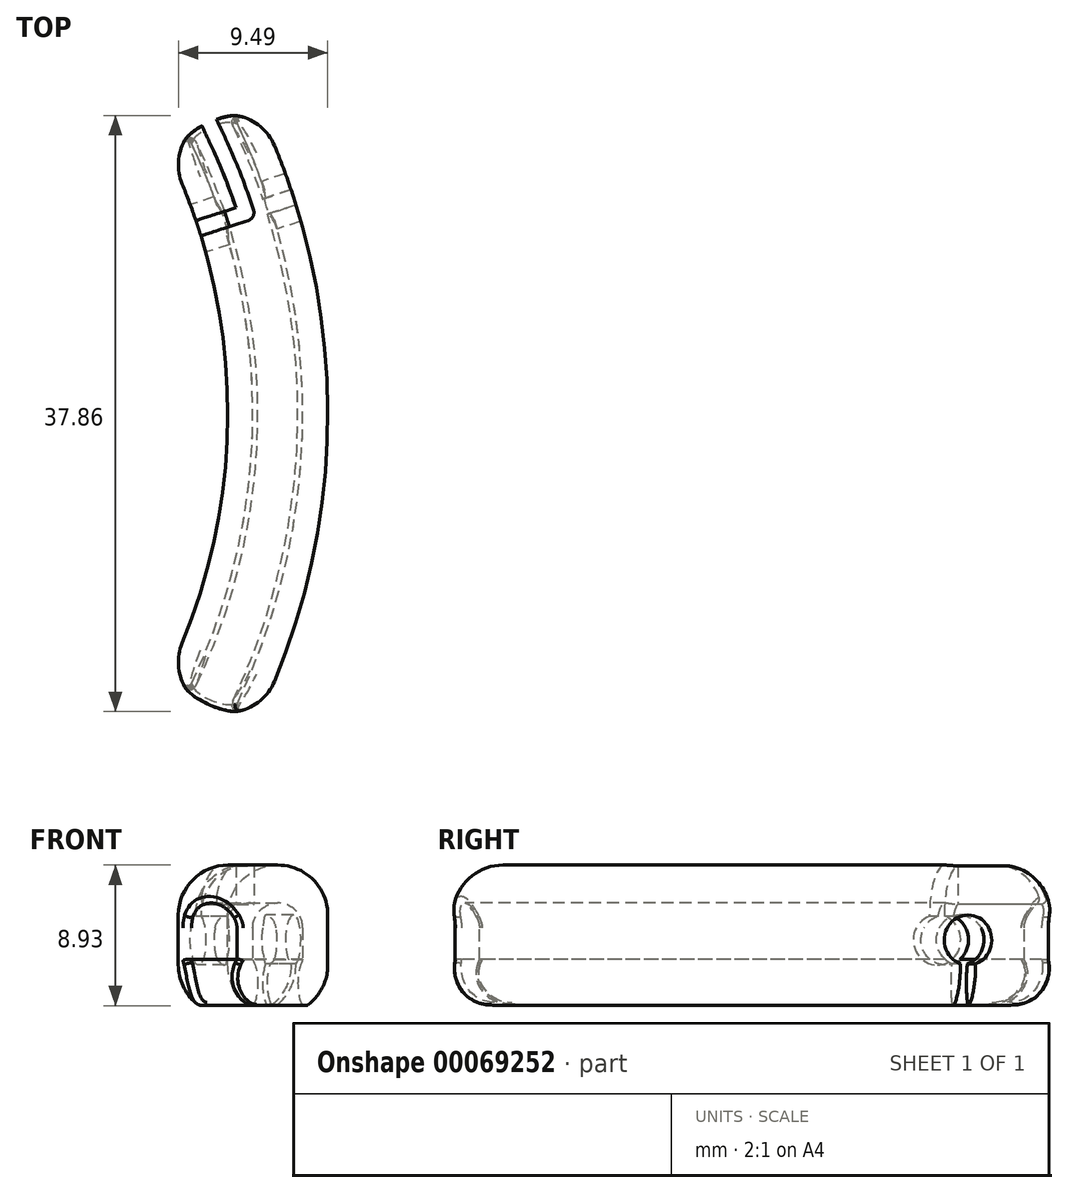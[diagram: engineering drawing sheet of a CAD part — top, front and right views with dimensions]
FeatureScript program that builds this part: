
annotation { "Feature Type Name" : "Feature", "Feature Type Description" : "" }
export const myFeature = defineFeature(function(context is Context, id is Id, definition is map)
    precondition{}
    {
        {
            var Q0;
            Q0=qCreatedBy(makeId("Front.planeOp"),FACE);
            var sketch = newSketch(context, id + "F0", { "sketchPlane" : qUnion([Q0])});
            skLineSegment(sketch, "E0", {"start": v(38.1, -1.59) * mm, "end": v(38.1, 1.59) * mm});
            skLineSegment(sketch, "E1", {"start": v(44.45, 1.59) * mm, "end": v(44.45, -1.59) * mm});
            skArc(sketch, "E2", {"start": v(44.45, 1.59) * mm, "mid": v(41.28, 4.76) * mm, "end": v(38.1, 1.59) * mm});
            skArc(sketch, "E3", {"start": v(38.1, -1.59) * mm, "mid": v(41.28, -4.76) * mm, "end": v(44.45, -1.59) * mm});
            skLineSegment(sketch, "E4", {"start": v(0, 0) * mm, "end": v(0, -27.8) * mm});
            skSolve(sketch);
        }
        {
            var Q0;
            Q0=makeQuery(id+"F0.imprint","IMPRINT",FACE,{"disambiguationData":[TD([[makeQuery(id+"F0.imprint","IMPRINT",EDGE,{"derivedFrom":sQuery(id+"F0.wireOp",EDGE,"E0")}),-1.0]])]});
            var Q1;
            Q1=sQuery(id+"F0.wireOp",EDGE,"E4");
            revolve(context, id + "F1", {"entities" : qUnion([Q0]), "axis" : qUnion([Q1]), "revolveType" : RevolveType.SYMMETRIC, "angle" : 45 * degree});
        }
        {
            var Q0;
            Q0=makeQuery(id+"F1.opRevolve","CAP_FACE",FACE,{"disambiguationData":[OSD([sQuery(id+"F0.wireOp",EDGE,"E0"),sQuery(id+"F0.wireOp",EDGE,"E1"),sQuery(id+"F0.wireOp",EDGE,"E2"),sQuery(id+"F0.wireOp",EDGE,"E3")])],"isStart":false});
            var sketch = newSketch(context, id + "F2", { "sketchPlane" : qUnion([Q0])});
            skLineSegment(sketch, "E5", {"start": v(41.28, 4.76) * mm, "end": v(41.28, -4.76) * mm});
            skSolve(sketch);
        }
        {
            var Q0;
            Q0=qSketchRegion(id+"F2",true);
            var Q1;
            {var subQ0=sQuery(id+"F2.wireOp",EDGE,"E5");Q1=makeQuery(id+"F2.imprint","IMPRINT",FACE,{"disambiguationData":[TD([[makeQuery(id+"F2.imprint","IMPRINT",EDGE,{"derivedFrom":subQ0}),1.0]])]});}
            var Q2;
            Q2=sQuery(id+"F2.wireOp",EDGE,"E5");
            revolve(context, id + "F3", {"operationType" : NewBodyOperationType.ADD, "entities" : qUnion([Q0, Q1]), "axis" : qUnion([Q2]), "revolveType" : RevolveType.FULL});
        }
        {
            var Q0;
            Q0=makeQuery(id+"F1.opRevolve","CAP_FACE",FACE,{"disambiguationData":[OSD([sQuery(id+"F0.wireOp",EDGE,"E0"),sQuery(id+"F0.wireOp",EDGE,"E1"),sQuery(id+"F0.wireOp",EDGE,"E2"),sQuery(id+"F0.wireOp",EDGE,"E3")])],"isStart":true});
            var sketch = newSketch(context, id + "F4", { "sketchPlane" : qUnion([Q0])});
            skLineSegment(sketch, "E6", {"start": v(-41.28, 4.76) * mm, "end": v(-41.28, -4.76) * mm});
            skSolve(sketch);
        }
        {
            var Q0;
            Q0=qSketchRegion(id+"F4",true);
            var Q1;
            {var subQ0=sQuery(id+"F4.wireOp",EDGE,"E6");Q1=makeQuery(id+"F4.imprint","IMPRINT",FACE,{"disambiguationData":[TD([[makeQuery(id+"F4.imprint","IMPRINT",EDGE,{"derivedFrom":subQ0}),1.0]])]});}
            var Q2;
            Q2=sQuery(id+"F4.wireOp",EDGE,"E6");
            revolve(context, id + "F5", {"operationType" : NewBodyOperationType.ADD, "entities" : qUnion([Q0, Q1]), "axis" : qUnion([Q2]), "revolveType" : RevolveType.FULL});
        }
        {
            var Q0;
            Q0=qCreatedBy(makeId("Front.planeOp"),FACE);
            var sketch = newSketch(context, id + "F6", { "sketchPlane" : qUnion([Q0])});
            skLineSegment(sketch, "E7", {"start": v(38.13, 4.76) * mm, "end": v(41.28, 4.76) * mm});
            skArc(sketch, "E8", {"start": v(41.28, 4.76) * mm, "mid": v(39.03, 3.83) * mm, "end": v(38.1, 1.59) * mm});
            skLineSegment(sketch, "E9", {"start": v(44.45, 1.59) * mm, "end": v(44.45, -1.59) * mm});
            skLineSegment(sketch, "E10", {"start": v(38.13, -4.76) * mm, "end": v(41.28, -4.76) * mm});
            skArc(sketch, "E11", {"start": v(38.1, -1.59) * mm, "mid": v(39.03, -3.83) * mm, "end": v(41.28, -4.76) * mm});
            skLineSegment(sketch, "E12", {"start": v(41.28, 4.76) * mm, "end": v(41.28, -4.76) * mm, "construction": true});
            skLineSegment(sketch, "E13", {"start": v(0, 0) * mm, "end": v(48.62, 0) * mm, "construction": true});
            skPoint(sketch, "E13.endSnap0", {"position": v(44.45, 0) * mm});
            skLineSegment(sketch, "E14", {"start": v(39.69, -6.35) * mm, "end": v(39.69, 0.76) * mm});
            skLineSegment(sketch, "E15", {"start": v(42.86, -6.35) * mm, "end": v(42.86, 0.76) * mm});
            skLineSegment(sketch, "E16", {"start": v(39.69, -6.35) * mm, "end": v(42.86, -6.35) * mm});
            skArc(sketch, "E17", {"start": v(42.86, 0.76) * mm, "mid": v(41.28, 2.35) * mm, "end": v(39.69, 0.76) * mm});
            skLineSegment(sketch, "E18", {"start": v(0, 0) * mm, "end": v(0, -11.33) * mm, "construction": true});
            skArc(sketch, "E19", {"start": v(39.69, -4.28) * mm, "mid": v(40, -2.76) * mm, "end": v(39.69, -1.23) * mm});
            skArc(sketch, "E20", {"start": v(42.86, -1.23) * mm, "mid": v(42.55, -2.76) * mm, "end": v(42.86, -4.28) * mm});
            skLineSegment(sketch, "E21", {"start": v(39.69, -1.23) * mm, "end": v(42.86, -1.23) * mm, "construction": true});
            skLineSegment(sketch, "E22", {"start": v(39.69, -4.28) * mm, "end": v(42.86, -4.28) * mm, "construction": true});
            skSolve(sketch);
        }
        {
            var Q0;
            {var subQ0=sQuery(id+"F6.wireOp",EDGE,"E11");var subQ1=sQuery(id+"F6.wireOp",EDGE,"E10");var subQ2=makeQuery(id+"F6.imprint","INTERSECT",VERTEX,{"derivedFrom":[subQ1,subQ0]});Q0=makeQuery(id+"F6.imprint","IMPRINT",FACE,{"disambiguationData":[TD([[makeQuery(id+"F6.imprint","IMPRINT",EDGE,{"disambiguationData":[TD([[subQ2,1.0]])],"derivedFrom":subQ1}),1.0]])]});}
            var Q1;
            Q1=makeQuery(id+"F6.imprint","IMPRINT",FACE,{"disambiguationData":[TD([[makeQuery(id+"F6.imprint","IMPRINT",EDGE,{"derivedFrom":sQuery(id+"F6.wireOp",EDGE,"E15")}),1.0]])]});
            var Q2;
            Q2=sQuery(id+"F6.wireOp",EDGE,"E18");
            revolve(context, id + "F7", {"operationType" : NewBodyOperationType.REMOVE, "entities" : qUnion([Q0, Q1]), "axis" : qUnion([Q2]), "revolveType" : RevolveType.FULL, "oppositeDirection" : true});
        }
        {
            var Q0;
            Q0=qCreatedBy(makeId("Top.planeOp"),FACE);
            var sketch = newSketch(context, id + "F8", { "sketchPlane" : qUnion([Q0])});
            skArc(sketch, "E23.0", {"start": v(41.07, -17.01) * mm, "mid": v(44.45, 0) * mm, "end": v(41.07, 17.01) * mm});
            skLineSegment(sketch, "E24.0", {"start": v(41.07, 17.01) * mm, "end": v(35.2, 14.58) * mm});
            skFitSpline(sketch, "E25.0", {"points": [v(35.7, 17.84) * mm, v(35.8, 17.96) * mm, v(35.96, 18.09) * mm, v(36.16, 18.22) * mm, v(36.37, 18.36) * mm, v(36.6, 18.48) * mm, v(36.85, 18.6) * mm, v(37.1, 18.72) * mm, v(37.35, 18.8) * mm, v(37.59, 18.87) * mm, v(37.82, 18.94) * mm, v(38.02, 18.97) * mm, v(38.18, 18.97) * mm]});
            skPoint(sketch, "E26.startSnap0", {"position": v(38.13, 15.8) * mm});
            skCircle(sketch, "E27", {"center": v(0, 0) * mm, "radius": 41.28 * mm, "construction": true});
            skLineSegment(sketch, "E28", {"start": v(0, 0) * mm, "end": v(47.07, 15.3) * mm, "construction": true});
            skArc(sketch, "E29", {"start": v(38.77, 12.6) * mm, "mid": v(37.24, 16.58) * mm, "end": v(35.3, 20.38) * mm});
            skArc(sketch, "E30", {"start": v(39.74, 12.91) * mm, "mid": v(38.17, 17) * mm, "end": v(36.19, 20.9) * mm});
            skArc(sketch, "E31", {"start": v(38.77, 12.6) * mm, "mid": v(39.41, 12.27) * mm, "end": v(39.74, 12.91) * mm});
            skLineSegment(sketch, "E32", {"start": v(35.3, 20.38) * mm, "end": v(36.19, 20.9) * mm});
            skSolve(sketch);
        }
        {
            var Q0;
            Q0=qSketchRegion(id+"F8",true);
            extrude(context, id + "F9", {"entities" : qUnion([Q0]), "operationType" : NewBodyOperationType.REMOVE, "endBound" : BoundingType.THROUGH_ALL, "depth" : 25.4 * mm});
        }
        {
            var Q0;
            Q0=sQuery(id+"F8.wireOp",VERTEX,"E30.center");
            var Q1;
            Q1=sQuery(id+"F8.wireOp",EDGE,"E28");
            cPlane(context, id + "F10", {"entities" : qUnion([Q0, Q1]), "cplaneType" : CPlaneType.LINE_POINT, "offset" : 152.4 * mm, "width" : 152.4 * mm, "height" : 152.4 * mm});
        }
        {
            var Q0;
            Q0=qCreatedBy(id+"F10.planeOp",FACE);
            var sketch = newSketch(context, id + "F11", { "sketchPlane" : qUnion([Q0])});
            skPoint(sketch, "E33", {"position": v(0, 0) * mm});
            skSolve(sketch);
        }
        {
            var Q0;
            Q0=sQuery(id+"F11.wireOp",VERTEX,"E33");
            var Q1;
            Q1=makeQuery(id+"F1.opRevolve","SWEPT_BODY",BODY,{"disambiguationData":[OSD([sQuery(id+"F0.wireOp",EDGE,"E0"),sQuery(id+"F0.wireOp",EDGE,"E1"),sQuery(id+"F0.wireOp",EDGE,"E2"),sQuery(id+"F0.wireOp",EDGE,"E3")])]});
            hole(context, id + "F12", {"style" : HoleStyle.SIMPLE, "holeDiameter" : 3.17 * mm, "endStyle" : HoleEndStyle.THROUGH, "oppositeDirection" : true, "locations" : qUnion([Q0]), "scope" : qUnion([Q1])});
        }
        {
            var Q0;
            Q0=qCreatedBy(makeId("Top.planeOp"),FACE);
            var sketch = newSketch(context, id + "F13", { "sketchPlane" : qUnion([Q0])});
            skArc(sketch, "E34.0", {"start": v(38.77, 12.6) * mm, "mid": v(39.41, 12.27) * mm, "end": v(39.74, 12.91) * mm});
            skLineSegment(sketch, "E35", {"start": v(40.25, 14.75) * mm, "end": v(41.76, 15.24) * mm});
            skLineSegment(sketch, "E36", {"start": v(42.74, 12.22) * mm, "end": v(41.23, 11.73) * mm});
            skLineSegment(sketch, "E37", {"start": v(35.71, 13.27) * mm, "end": v(37.22, 13.76) * mm});
            skLineSegment(sketch, "E38", {"start": v(38.2, 10.74) * mm, "end": v(36.7, 10.25) * mm});
            skLineSegment(sketch, "E39", {"start": v(35.47, 12.06) * mm, "end": v(39.1, 13.24) * mm});
            skLineSegment(sketch, "E40", {"start": v(39.1, 13.24) * mm, "end": v(39.41, 12.27) * mm});
            skLineSegment(sketch, "E41", {"start": v(39.41, 12.27) * mm, "end": v(35.78, 11.1) * mm});
            skLineSegment(sketch, "E42", {"start": v(35.78, 11.1) * mm, "end": v(35.47, 12.06) * mm});
            skLineSegment(sketch, "E43", {"start": v(35.63, 11.58) * mm, "end": v(39.25, 12.75) * mm, "construction": true});
            skSolve(sketch);
        }
        {
            var Q0;
            Q0=qSketchRegion(id+"F13",true);
            extrude(context, id + "F14", {"entities" : qUnion([Q0]), "operationType" : NewBodyOperationType.REMOVE, "endBound" : BoundingType.THROUGH_ALL, "depth" : 25.4 * mm});
        }
        {
            var Q0;
            Q0=qCreatedBy(makeId("Top.planeOp"),FACE);
            var sketch = newSketch(context, id + "F15", { "sketchPlane" : qUnion([Q0])});
            skLineSegment(sketch, "E44", {"start": v(39.1, 13.24) * mm, "end": v(39.41, 12.27) * mm});
            skLineSegment(sketch, "E45", {"start": v(39.41, 12.27) * mm, "end": v(43.04, 13.45) * mm});
            skLineSegment(sketch, "E46", {"start": v(43.04, 13.45) * mm, "end": v(42.72, 14.42) * mm});
            skLineSegment(sketch, "E47", {"start": v(42.72, 14.42) * mm, "end": v(39.1, 13.24) * mm});
            skSolve(sketch);
        }
        {
            var Q0;
            Q0=qSketchRegion(id+"F15",true);
            extrude(context, id + "F16", {"entities" : qUnion([Q0]), "operationType" : NewBodyOperationType.REMOVE, "endBound" : BoundingType.THROUGH_ALL, "oppositeDirection" : true, "depth" : 25.4 * mm});
        }
        {
            var Q0;
            {var subQ0=sQuery(id+"F0.wireOp",EDGE,"E3");var subQ1=makeQuery(id+"F1.opRevolve","SWEPT_FACE",FACE,{"disambiguationData":[OSD([subQ0])]});var subQ2=sQuery(id+"F6.wireOp",EDGE,"E15");var subQ3=makeQuery(id+"F7.opRevolve","SWEPT_FACE",FACE,{"disambiguationData":[OSD([subQ2]),TDD([makeQuery(id+"F6.imprint","IMPRINT",EDGE,{"disambiguationData":[TD([[makeQuery(id+"F6.imprint","INTERSECT",VERTEX,{"derivedFrom":[subQ2,sQuery(id+"F6.wireOp",EDGE,"E16")]}),-1.0]])],"derivedFrom":subQ2})])]});Q0=makeQuery(id+"F16.boolean.opBoolean","SPLIT",EDGE,{"disambiguationData":[TD([makeQuery(id+"F3.opRevolve","SWEPT_FACE",FACE,{"disambiguationData":[OSD([subQ0])]})])],"derivedFrom":makeQuery(id+"F7.boolean.opBoolean","INTERSECT",EDGE,{"derivedFrom":[subQ1,subQ3]})});}
            var Q1;
            {var subQ0=sQuery(id+"F0.wireOp",EDGE,"E3");var subQ1=makeQuery(id+"F1.opRevolve","SWEPT_FACE",FACE,{"disambiguationData":[OSD([subQ0])]});var subQ2=sQuery(id+"F6.wireOp",EDGE,"E15");var subQ3=makeQuery(id+"F7.opRevolve","SWEPT_FACE",FACE,{"disambiguationData":[OSD([subQ2]),TDD([makeQuery(id+"F6.imprint","IMPRINT",EDGE,{"disambiguationData":[TD([[makeQuery(id+"F6.imprint","INTERSECT",VERTEX,{"derivedFrom":[subQ2,sQuery(id+"F6.wireOp",EDGE,"E16")]}),-1.0]])],"derivedFrom":subQ2})])]});Q1=makeQuery(id+"F16.boolean.opBoolean","SPLIT",EDGE,{"disambiguationData":[TD([makeQuery(id+"F5.opRevolve","SWEPT_FACE",FACE,{"disambiguationData":[OSD([subQ0])]})])],"derivedFrom":makeQuery(id+"F7.boolean.opBoolean","INTERSECT",EDGE,{"derivedFrom":[subQ1,subQ3]})});}
            var Q2;
            {var subQ0=sQuery(id+"F6.wireOp",EDGE,"E15");Q2=makeQuery(id+"F7.boolean.opBoolean","INTERSECT",EDGE,{"derivedFrom":[makeQuery(id+"F5.opRevolve","SWEPT_FACE",FACE,{"disambiguationData":[OSD([sQuery(id+"F0.wireOp",EDGE,"E3")])]}),makeQuery(id+"F7.opRevolve","SWEPT_FACE",FACE,{"disambiguationData":[OSD([subQ0]),TDD([makeQuery(id+"F6.imprint","IMPRINT",EDGE,{"disambiguationData":[TD([[makeQuery(id+"F6.imprint","INTERSECT",VERTEX,{"derivedFrom":[subQ0,sQuery(id+"F6.wireOp",EDGE,"E16")]}),-1.0]])],"derivedFrom":subQ0})])]})]});}
            var Q3;
            {var subQ0=sQuery(id+"F6.wireOp",EDGE,"E14");var subQ2=makeQuery(id+"F6.imprint","INTERSECT",VERTEX,{"derivedFrom":[sQuery(id+"F6.wireOp",EDGE,"E10"),subQ0]});Q3=makeQuery(id+"F7.boolean.opBoolean","INTERSECT",EDGE,{"derivedFrom":[makeQuery(id+"F5.opRevolve","SWEPT_FACE",FACE,{"disambiguationData":[OSD([sQuery(id+"F0.wireOp",EDGE,"E3")])]}),makeQuery(id+"F7.opRevolve","SWEPT_FACE",FACE,{"disambiguationData":[OSD([subQ0]),TDD([makeQuery(id+"F6.imprint","IMPRINT",EDGE,{"disambiguationData":[TD([[makeQuery(id+"F6.imprint","INTERSECT",VERTEX,{"derivedFrom":[subQ0,sQuery(id+"F6.wireOp",EDGE,"E16")]}),-1.0]])],"derivedFrom":subQ0}),makeQuery(id+"F6.imprint","IMPRINT",EDGE,{"disambiguationData":[TD([[subQ2,-1.0]])],"derivedFrom":subQ0}),makeQuery(id+"F6.imprint","IMPRINT",EDGE,{"disambiguationData":[TD([[makeQuery(id+"F6.imprint","INTERSECT",VERTEX,{"disambiguationData":[OD(0.0)],"derivedFrom":[subQ0,sQuery(id+"F6.wireOp",EDGE,"E19")]}),1.0]])],"derivedFrom":subQ0})])]})]});}
            var Q4;
            {var subQ0=sQuery(id+"F6.wireOp",EDGE,"E14");var subQ2=makeQuery(id+"F6.imprint","INTERSECT",VERTEX,{"derivedFrom":[sQuery(id+"F6.wireOp",EDGE,"E10"),subQ0]});Q4=makeQuery(id+"F7.boolean.opBoolean","INTERSECT",EDGE,{"derivedFrom":[makeQuery(id+"F1.opRevolve","SWEPT_FACE",FACE,{"disambiguationData":[OSD([sQuery(id+"F0.wireOp",EDGE,"E3")])]}),makeQuery(id+"F7.opRevolve","SWEPT_FACE",FACE,{"disambiguationData":[OSD([subQ0]),TDD([makeQuery(id+"F6.imprint","IMPRINT",EDGE,{"disambiguationData":[TD([[makeQuery(id+"F6.imprint","INTERSECT",VERTEX,{"derivedFrom":[subQ0,sQuery(id+"F6.wireOp",EDGE,"E16")]}),-1.0]])],"derivedFrom":subQ0}),makeQuery(id+"F6.imprint","IMPRINT",EDGE,{"disambiguationData":[TD([[subQ2,-1.0]])],"derivedFrom":subQ0}),makeQuery(id+"F6.imprint","IMPRINT",EDGE,{"disambiguationData":[TD([[makeQuery(id+"F6.imprint","INTERSECT",VERTEX,{"disambiguationData":[OD(0.0)],"derivedFrom":[subQ0,sQuery(id+"F6.wireOp",EDGE,"E19")]}),1.0]])],"derivedFrom":subQ0})])]})]});}
            var Q5;
            {var subQ0=sQuery(id+"F6.wireOp",EDGE,"E14");var subQ2=makeQuery(id+"F6.imprint","INTERSECT",VERTEX,{"derivedFrom":[sQuery(id+"F6.wireOp",EDGE,"E10"),subQ0]});Q5=makeQuery(id+"F7.boolean.opBoolean","INTERSECT",EDGE,{"derivedFrom":[makeQuery(id+"F3.opRevolve","SWEPT_FACE",FACE,{"disambiguationData":[OSD([sQuery(id+"F0.wireOp",EDGE,"E3")])]}),makeQuery(id+"F7.opRevolve","SWEPT_FACE",FACE,{"disambiguationData":[OSD([subQ0]),TDD([makeQuery(id+"F6.imprint","IMPRINT",EDGE,{"disambiguationData":[TD([[makeQuery(id+"F6.imprint","INTERSECT",VERTEX,{"derivedFrom":[subQ0,sQuery(id+"F6.wireOp",EDGE,"E16")]}),-1.0]])],"derivedFrom":subQ0}),makeQuery(id+"F6.imprint","IMPRINT",EDGE,{"disambiguationData":[TD([[subQ2,-1.0]])],"derivedFrom":subQ0}),makeQuery(id+"F6.imprint","IMPRINT",EDGE,{"disambiguationData":[TD([[makeQuery(id+"F6.imprint","INTERSECT",VERTEX,{"disambiguationData":[OD(0.0)],"derivedFrom":[subQ0,sQuery(id+"F6.wireOp",EDGE,"E19")]}),1.0]])],"derivedFrom":subQ0})])]})]});}
            var Q6;
            {var subQ0=sQuery(id+"F6.wireOp",EDGE,"E15");Q6=makeQuery(id+"F7.boolean.opBoolean","INTERSECT",EDGE,{"derivedFrom":[makeQuery(id+"F3.opRevolve","SWEPT_FACE",FACE,{"disambiguationData":[OSD([sQuery(id+"F0.wireOp",EDGE,"E3")])]}),makeQuery(id+"F7.opRevolve","SWEPT_FACE",FACE,{"disambiguationData":[OSD([subQ0]),TDD([makeQuery(id+"F6.imprint","IMPRINT",EDGE,{"disambiguationData":[TD([[makeQuery(id+"F6.imprint","INTERSECT",VERTEX,{"derivedFrom":[subQ0,sQuery(id+"F6.wireOp",EDGE,"E16")]}),-1.0]])],"derivedFrom":subQ0})])]})]});}
            var Q7;
            Q7=makeQuery(id+"F7.boolean.opBoolean","INTERSECT",EDGE,{"derivedFrom":[makeQuery(id+"F3.opRevolve","SWEPT_FACE",FACE,{"disambiguationData":[OSD([sQuery(id+"F0.wireOp",EDGE,"E3")])]}),makeQuery(id+"F7.opRevolve","SWEPT_FACE",FACE,{"disambiguationData":[OSD([sQuery(id+"F6.wireOp",EDGE,"E20")])]})]});
            var Q8;
            Q8=makeQuery(id+"F7.boolean.opBoolean","INTERSECT",EDGE,{"derivedFrom":[makeQuery(id+"F3.opRevolve","SWEPT_FACE",FACE,{"disambiguationData":[OSD([sQuery(id+"F0.wireOp",EDGE,"E1")])]}),makeQuery(id+"F7.opRevolve","SWEPT_FACE",FACE,{"disambiguationData":[OSD([sQuery(id+"F6.wireOp",EDGE,"E20")])]})]});
            var Q9;
            {var subQ0=sQuery(id+"F6.wireOp",EDGE,"E15");Q9=makeQuery(id+"F7.boolean.opBoolean","INTERSECT",EDGE,{"derivedFrom":[makeQuery(id+"F3.opRevolve","SWEPT_FACE",FACE,{"disambiguationData":[OSD([sQuery(id+"F0.wireOp",EDGE,"E1")])]}),makeQuery(id+"F7.opRevolve","SWEPT_FACE",FACE,{"disambiguationData":[OSD([subQ0]),TDD([makeQuery(id+"F6.imprint","IMPRINT",EDGE,{"disambiguationData":[TD([[makeQuery(id+"F6.imprint","INTERSECT",VERTEX,{"derivedFrom":[subQ0,sQuery(id+"F6.wireOp",EDGE,"E17")]}),1.0]])],"derivedFrom":subQ0})])]})]});}
            var Q10;
            Q10=makeQuery(id+"F7.boolean.opBoolean","INTERSECT",EDGE,{"disambiguationData":[OD(1.0)],"derivedFrom":[makeQuery(id+"F3.opRevolve","SWEPT_FACE",FACE,{"disambiguationData":[OSD([sQuery(id+"F0.wireOp",EDGE,"E1")])]}),makeQuery(id+"F7.opRevolve","SWEPT_FACE",FACE,{"disambiguationData":[OSD([sQuery(id+"F6.wireOp",EDGE,"E17")])]})]});
            var Q11;
            Q11=makeQuery(id+"F7.boolean.opBoolean","INTERSECT",EDGE,{"derivedFrom":[makeQuery(id+"F3.opRevolve","SWEPT_FACE",FACE,{"disambiguationData":[OSD([sQuery(id+"F0.wireOp",EDGE,"E2")])]}),makeQuery(id+"F7.opRevolve","SWEPT_FACE",FACE,{"disambiguationData":[OSD([sQuery(id+"F6.wireOp",EDGE,"E17")])]})]});
            var Q12;
            Q12=makeQuery(id+"F7.boolean.opBoolean","INTERSECT",EDGE,{"disambiguationData":[OD(0.0)],"derivedFrom":[makeQuery(id+"F3.opRevolve","SWEPT_FACE",FACE,{"disambiguationData":[OSD([sQuery(id+"F0.wireOp",EDGE,"E1")])]}),makeQuery(id+"F7.opRevolve","SWEPT_FACE",FACE,{"disambiguationData":[OSD([sQuery(id+"F6.wireOp",EDGE,"E17")])]})]});
            var Q13;
            {var subQ0=sQuery(id+"F6.wireOp",EDGE,"E14");Q13=makeQuery(id+"F7.boolean.opBoolean","INTERSECT",EDGE,{"derivedFrom":[makeQuery(id+"F3.opRevolve","SWEPT_FACE",FACE,{"disambiguationData":[OSD([sQuery(id+"F0.wireOp",EDGE,"E1")])]}),makeQuery(id+"F7.opRevolve","SWEPT_FACE",FACE,{"disambiguationData":[OSD([subQ0]),TDD([makeQuery(id+"F6.imprint","IMPRINT",EDGE,{"disambiguationData":[TD([[makeQuery(id+"F6.imprint","INTERSECT",VERTEX,{"derivedFrom":[subQ0,sQuery(id+"F6.wireOp",EDGE,"E17")]}),1.0]])],"derivedFrom":subQ0})])]})]});}
            var Q14;
            Q14=makeQuery(id+"F7.boolean.opBoolean","INTERSECT",EDGE,{"derivedFrom":[makeQuery(id+"F3.opRevolve","SWEPT_FACE",FACE,{"disambiguationData":[OSD([sQuery(id+"F0.wireOp",EDGE,"E1")])]}),makeQuery(id+"F7.opRevolve","SWEPT_FACE",FACE,{"disambiguationData":[OSD([sQuery(id+"F6.wireOp",EDGE,"E19")])]})]});
            var Q15;
            Q15=makeQuery(id+"F7.boolean.opBoolean","INTERSECT",EDGE,{"derivedFrom":[makeQuery(id+"F3.opRevolve","SWEPT_FACE",FACE,{"disambiguationData":[OSD([sQuery(id+"F0.wireOp",EDGE,"E3")])]}),makeQuery(id+"F7.opRevolve","SWEPT_FACE",FACE,{"disambiguationData":[OSD([sQuery(id+"F6.wireOp",EDGE,"E19")])]})]});
            var Q16;
            Q16=makeQuery(id+"F7.boolean.opBoolean","INTERSECT",EDGE,{"derivedFrom":[makeQuery(id+"F5.opRevolve","SWEPT_FACE",FACE,{"disambiguationData":[OSD([sQuery(id+"F0.wireOp",EDGE,"E3")])]}),makeQuery(id+"F7.opRevolve","SWEPT_FACE",FACE,{"disambiguationData":[OSD([sQuery(id+"F6.wireOp",EDGE,"E19")])]})]});
            var Q17;
            Q17=makeQuery(id+"F7.boolean.opBoolean","INTERSECT",EDGE,{"derivedFrom":[makeQuery(id+"F5.opRevolve","SWEPT_FACE",FACE,{"disambiguationData":[OSD([sQuery(id+"F0.wireOp",EDGE,"E0")])]}),makeQuery(id+"F7.opRevolve","SWEPT_FACE",FACE,{"disambiguationData":[OSD([sQuery(id+"F6.wireOp",EDGE,"E19")])]})]});
            var Q18;
            {var subQ0=sQuery(id+"F6.wireOp",EDGE,"E14");Q18=makeQuery(id+"F7.boolean.opBoolean","INTERSECT",EDGE,{"derivedFrom":[makeQuery(id+"F5.opRevolve","SWEPT_FACE",FACE,{"disambiguationData":[OSD([sQuery(id+"F0.wireOp",EDGE,"E0")])]}),makeQuery(id+"F7.opRevolve","SWEPT_FACE",FACE,{"disambiguationData":[OSD([subQ0]),TDD([makeQuery(id+"F6.imprint","IMPRINT",EDGE,{"disambiguationData":[TD([[makeQuery(id+"F6.imprint","INTERSECT",VERTEX,{"derivedFrom":[subQ0,sQuery(id+"F6.wireOp",EDGE,"E17")]}),1.0]])],"derivedFrom":subQ0})])]})]});}
            var Q19;
            Q19=makeQuery(id+"F7.boolean.opBoolean","INTERSECT",EDGE,{"derivedFrom":[makeQuery(id+"F5.opRevolve","SWEPT_FACE",FACE,{"disambiguationData":[OSD([sQuery(id+"F0.wireOp",EDGE,"E3")])]}),makeQuery(id+"F7.opRevolve","SWEPT_FACE",FACE,{"disambiguationData":[OSD([sQuery(id+"F6.wireOp",EDGE,"E20")])]})]});
            var Q20;
            Q20=makeQuery(id+"F7.boolean.opBoolean","INTERSECT",EDGE,{"derivedFrom":[makeQuery(id+"F5.opRevolve","SWEPT_FACE",FACE,{"disambiguationData":[OSD([sQuery(id+"F0.wireOp",EDGE,"E0")])]}),makeQuery(id+"F7.opRevolve","SWEPT_FACE",FACE,{"disambiguationData":[OSD([sQuery(id+"F6.wireOp",EDGE,"E20")])]})]});
            var Q21;
            {var subQ0=sQuery(id+"F6.wireOp",EDGE,"E15");Q21=makeQuery(id+"F7.boolean.opBoolean","INTERSECT",EDGE,{"derivedFrom":[makeQuery(id+"F5.opRevolve","SWEPT_FACE",FACE,{"disambiguationData":[OSD([sQuery(id+"F0.wireOp",EDGE,"E0")])]}),makeQuery(id+"F7.opRevolve","SWEPT_FACE",FACE,{"disambiguationData":[OSD([subQ0]),TDD([makeQuery(id+"F6.imprint","IMPRINT",EDGE,{"disambiguationData":[TD([[makeQuery(id+"F6.imprint","INTERSECT",VERTEX,{"derivedFrom":[subQ0,sQuery(id+"F6.wireOp",EDGE,"E17")]}),1.0]])],"derivedFrom":subQ0})])]})]});}
            var Q22;
            Q22=makeQuery(id+"F7.boolean.opBoolean","INTERSECT",EDGE,{"disambiguationData":[OD(1.0)],"derivedFrom":[makeQuery(id+"F5.opRevolve","SWEPT_FACE",FACE,{"disambiguationData":[OSD([sQuery(id+"F0.wireOp",EDGE,"E0")])]}),makeQuery(id+"F7.opRevolve","SWEPT_FACE",FACE,{"disambiguationData":[OSD([sQuery(id+"F6.wireOp",EDGE,"E17")])]})]});
            var Q23;
            {var subQ0=makeQuery(id+"F5.opRevolve","SWEPT_FACE",FACE,{"disambiguationData":[OSD([sQuery(id+"F0.wireOp",EDGE,"E2")])]});var subQ1=makeQuery(id+"F7.opRevolve","SWEPT_FACE",FACE,{"disambiguationData":[OSD([sQuery(id+"F6.wireOp",EDGE,"E17")])]});Q23=makeQuery(id+"F9.boolean.opBoolean","SPLIT",EDGE,{"disambiguationData":[TD([makeQuery(id+"F9.opExtrude","SWEPT_FACE",FACE,{"disambiguationData":[OSD([sQuery(id+"F8.wireOp",EDGE,"E30")])]})])],"derivedFrom":makeQuery(id+"F7.boolean.opBoolean","INTERSECT",EDGE,{"derivedFrom":[subQ0,subQ1]})});}
            var Q24;
            Q24=makeQuery(id+"F7.boolean.opBoolean","INTERSECT",EDGE,{"disambiguationData":[OD(0.0)],"derivedFrom":[makeQuery(id+"F5.opRevolve","SWEPT_FACE",FACE,{"disambiguationData":[OSD([sQuery(id+"F0.wireOp",EDGE,"E0")])]}),makeQuery(id+"F7.opRevolve","SWEPT_FACE",FACE,{"disambiguationData":[OSD([sQuery(id+"F6.wireOp",EDGE,"E17")])]})]});
            var Q25;
            {var subQ0=makeQuery(id+"F5.opRevolve","SWEPT_FACE",FACE,{"disambiguationData":[OSD([sQuery(id+"F0.wireOp",EDGE,"E2")])]});var subQ1=makeQuery(id+"F7.opRevolve","SWEPT_FACE",FACE,{"disambiguationData":[OSD([sQuery(id+"F6.wireOp",EDGE,"E17")])]});Q25=makeQuery(id+"F9.boolean.opBoolean","SPLIT",EDGE,{"disambiguationData":[TD([makeQuery(id+"F9.opExtrude","SWEPT_FACE",FACE,{"disambiguationData":[OSD([sQuery(id+"F8.wireOp",EDGE,"E29")])]})])],"derivedFrom":makeQuery(id+"F7.boolean.opBoolean","INTERSECT",EDGE,{"derivedFrom":[subQ0,subQ1]})});}
            fillet(context, id + "F17", {"entities" : qUnion([Q0, Q1, Q2, Q3, Q4, Q5, Q6, Q7, Q8, Q9, Q10, Q11, Q12, Q13, Q14, Q15, Q16, Q17, Q18, Q19, Q20, Q21, Q22, Q23, Q24, Q25]), "radius" : 0.3 * mm, "allowEdgeOverflow" : false});
        }
        {
            var Q0;
            Q0=qCreatedBy(makeId("Right.planeOp"),FACE);
            cPlane(context, id + "F18", {"entities" : qUnion([Q0]), "cplaneType" : CPlaneType.OFFSET, "offset" : 44.45 * mm, "width" : 152.4 * mm, "height" : 152.4 * mm});
        }
    });
